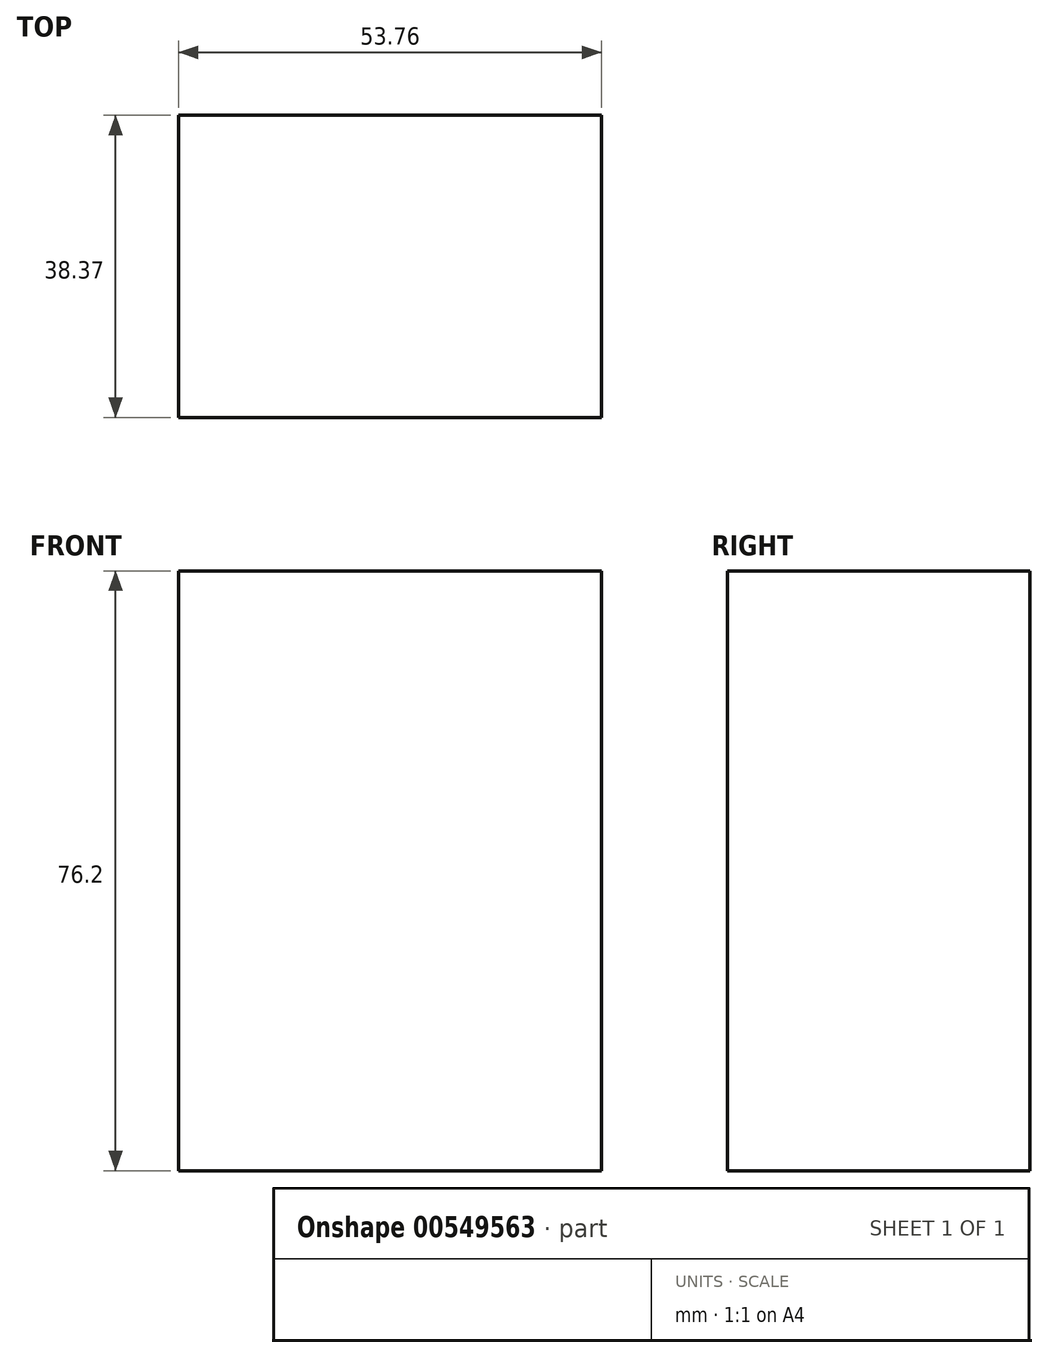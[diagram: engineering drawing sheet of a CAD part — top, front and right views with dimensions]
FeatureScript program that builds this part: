
annotation { "Feature Type Name" : "Feature", "Feature Type Description" : "" }
export const myFeature = defineFeature(function(context is Context, id is Id, definition is map)
    precondition{}
    {
        {
            var Q0;
            Q0=qCreatedBy(makeId("Top.planeOp"),FACE);
            var sketch = newSketch(context, id + "F0", { "sketchPlane" : qUnion([Q0])});
            skLineSegment(sketch, "E0.bottom", {"start": v(0, 38.37) * mm, "end": v(53.76, 38.37) * mm});
            skLineSegment(sketch, "E0.top", {"start": v(0, 0) * mm, "end": v(53.76, 0) * mm});
            skLineSegment(sketch, "E0.left", {"start": v(0, 38.37) * mm, "end": v(0, 0) * mm});
            skLineSegment(sketch, "E0.right", {"start": v(53.76, 38.37) * mm, "end": v(53.76, 0) * mm});
            skSolve(sketch);
        }
        {
            var Q0;
            Q0 = qSketchRegion(id + "F0", true);
            extrude(context, id + "F1", {"entities" : qUnion([Q0]), "depth" : 76.2 * mm, "offsetDistance" : 25.4 * mm});
        }
    });
